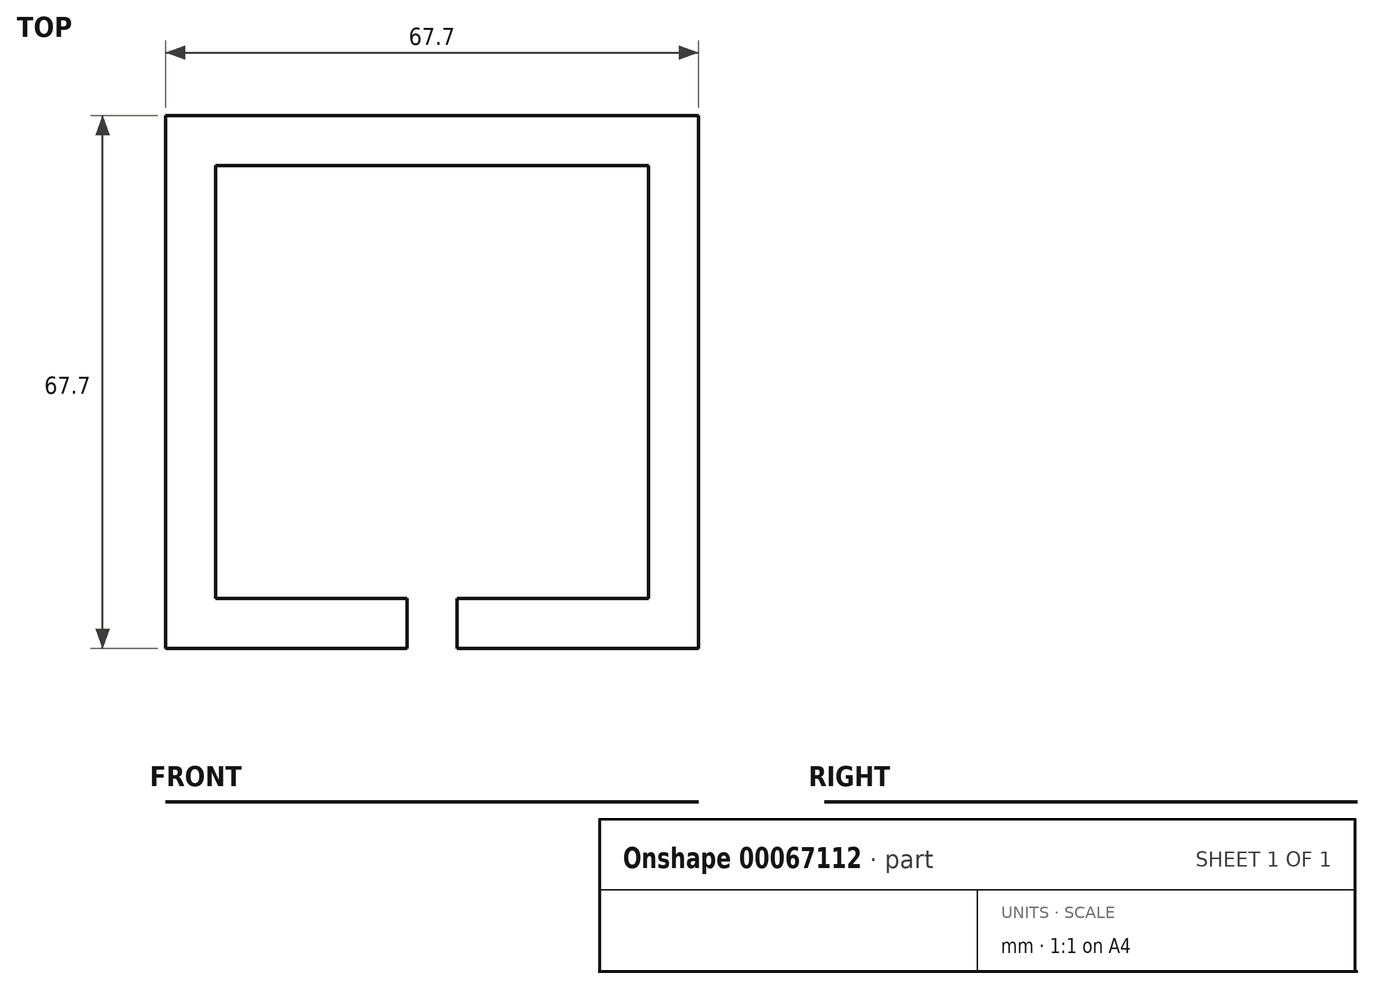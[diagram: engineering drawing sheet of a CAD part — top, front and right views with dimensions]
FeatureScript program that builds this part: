
annotation { "Feature Type Name" : "Feature", "Feature Type Description" : "" }
export const myFeature = defineFeature(function(context is Context, id is Id, definition is map)
    precondition{}
    {
        {
            var Q0;
            Q0=qCreatedBy(makeId("Top.planeOp"),FACE);
            var sketch = newSketch(context, id + "F0", { "sketchPlane" : qUnion([Q0])});
            skLineSegment(sketch, "E0.bottom", {"start": v(-33.85, 0) * mm, "end": v(33.85, 0) * mm});
            skLineSegment(sketch, "E0.top", {"start": v(-33.85, -67.7) * mm, "end": v(33.85, -67.7) * mm});
            skLineSegment(sketch, "E0.left", {"start": v(-33.85, 0) * mm, "end": v(-33.85, -67.7) * mm});
            skLineSegment(sketch, "E0.right", {"start": v(33.85, 0) * mm, "end": v(33.85, -67.7) * mm});
            skLineSegment(sketch, "E1.bottom", {"start": v(-27.5, -6.35) * mm, "end": v(27.5, -6.35) * mm});
            skLineSegment(sketch, "E1.top", {"start": v(-27.5, -61.35) * mm, "end": v(27.5, -61.35) * mm});
            skLineSegment(sketch, "E1.left", {"start": v(-27.5, -6.35) * mm, "end": v(-27.5, -61.35) * mm});
            skLineSegment(sketch, "E1.right", {"start": v(27.5, -6.35) * mm, "end": v(27.5, -61.35) * mm});
            skLineSegment(sketch, "E2", {"start": v(-27.5, -6.35) * mm, "end": v(-33.85, -6.35) * mm, "construction": true});
            skLineSegment(sketch, "E3", {"start": v(27.5, -6.35) * mm, "end": v(33.85, -6.35) * mm, "construction": true});
            skLineSegment(sketch, "E4", {"start": v(0, 0) * mm, "end": v(0, -6.35) * mm, "construction": true});
            skLineSegment(sketch, "E5.bottom", {"start": v(-3.17, -61.35) * mm, "end": v(3.17, -61.35) * mm});
            skLineSegment(sketch, "E5.top", {"start": v(-3.17, -67.7) * mm, "end": v(3.17, -67.7) * mm});
            skLineSegment(sketch, "E5.left", {"start": v(-3.17, -61.35) * mm, "end": v(-3.17, -67.7) * mm});
            skLineSegment(sketch, "E5.right", {"start": v(3.18, -61.35) * mm, "end": v(3.18, -67.7) * mm});
            skLineSegment(sketch, "E6", {"start": v(-3.17, -64.52) * mm, "end": v(-33.85, -64.52) * mm, "construction": true});
            skLineSegment(sketch, "E7", {"start": v(3.17, -64.52) * mm, "end": v(33.85, -64.52) * mm, "construction": true});
            skSolve(sketch);
        }
        {
            var Q0;
            Q0=makeQuery(id+"F0.imprint","IMPRINT",FACE,{"disambiguationData":[TD([[makeQuery(id+"F0.imprint","IMPRINT",EDGE,{"derivedFrom":sQuery(id+"F0.wireOp",EDGE,"E0.bottom")}),-1.0]])]});
            extrude(context, id + "F1", {"entities" : qUnion([Q0]), "depth" : 1 / 203.2 * mm});
        }
    });
